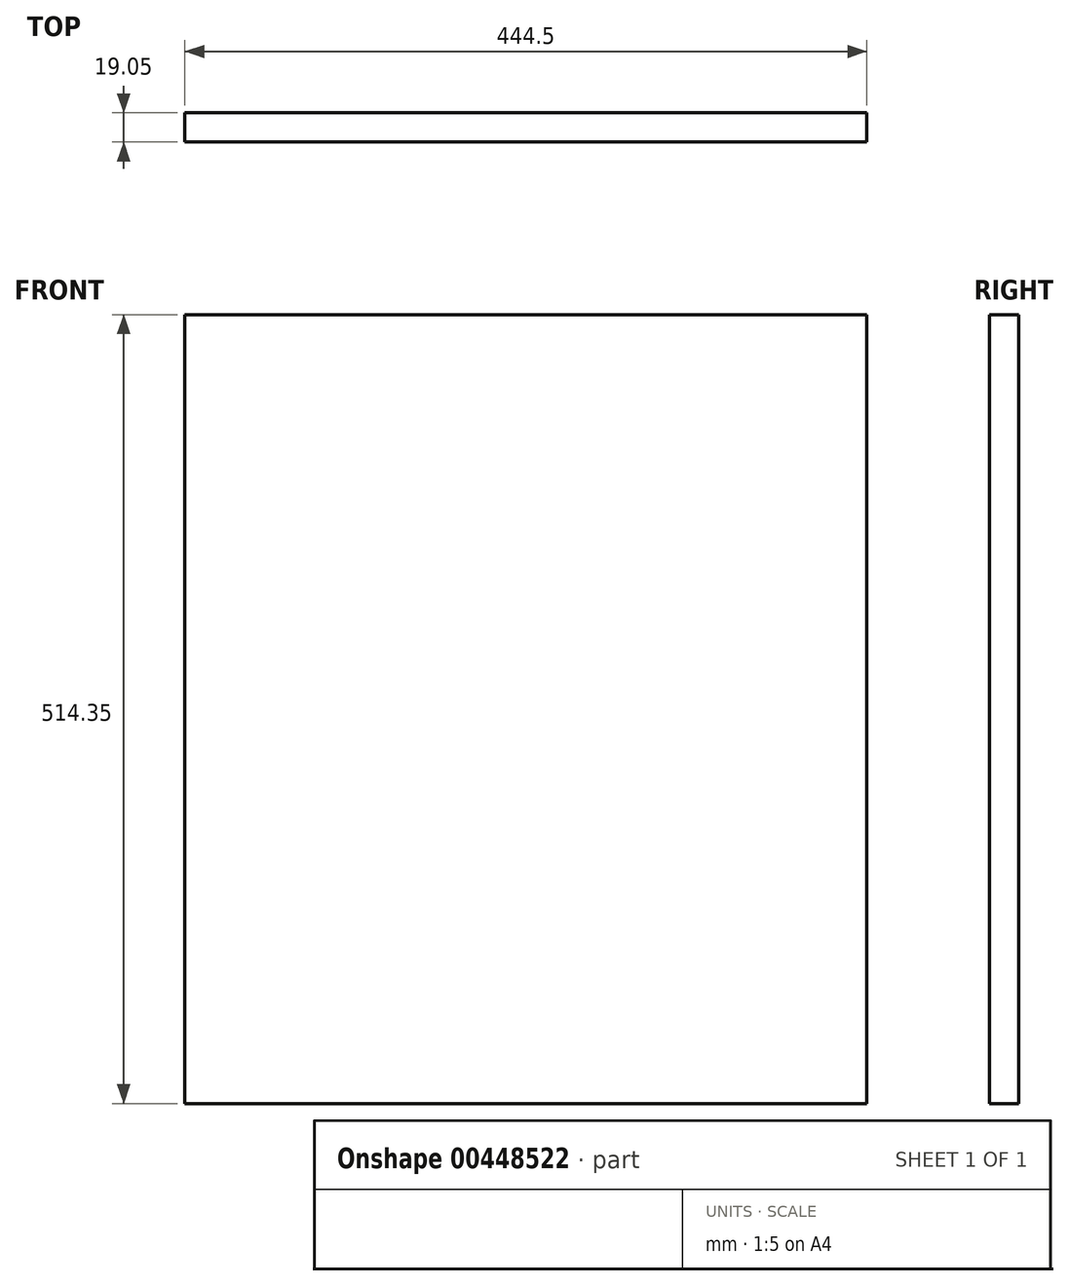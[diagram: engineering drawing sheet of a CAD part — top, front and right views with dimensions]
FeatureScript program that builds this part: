
annotation { "Feature Type Name" : "Feature", "Feature Type Description" : "" }
export const myFeature = defineFeature(function(context is Context, id is Id, definition is map)
    precondition{}
    {
        {
            var Q0;
            Q0=qCreatedBy(makeId("Front.planeOp"),FACE);
            var sketch = newSketch(context, id + "F0", { "sketchPlane" : qUnion([Q0])});
            skLineSegment(sketch, "E0.bottom", {"start": v(0, 0) * mm, "end": v(444.5, 0) * mm});
            skLineSegment(sketch, "E0.top", {"start": v(0, 514.35) * mm, "end": v(444.5, 514.35) * mm});
            skLineSegment(sketch, "E0.left", {"start": v(0, 0) * mm, "end": v(0, 514.35) * mm});
            skLineSegment(sketch, "E0.right", {"start": v(444.5, 0) * mm, "end": v(444.5, 514.35) * mm});
            skSolve(sketch);
        }
        {
            var Q0;
            Q0=makeQuery(id+"F0.imprint","IMPRINT",FACE,{"disambiguationData":[TD([[makeQuery(id+"F0.imprint","IMPRINT",EDGE,{"derivedFrom":sQuery(id+"F0.wireOp",EDGE,"E0.bottom")}),1.0]])]});
            extrude(context, id + "F1", {"entities" : qUnion([Q0]), "depth" : 19.05 * mm, "offsetDistance" : 25.4 * mm});
        }
    });
